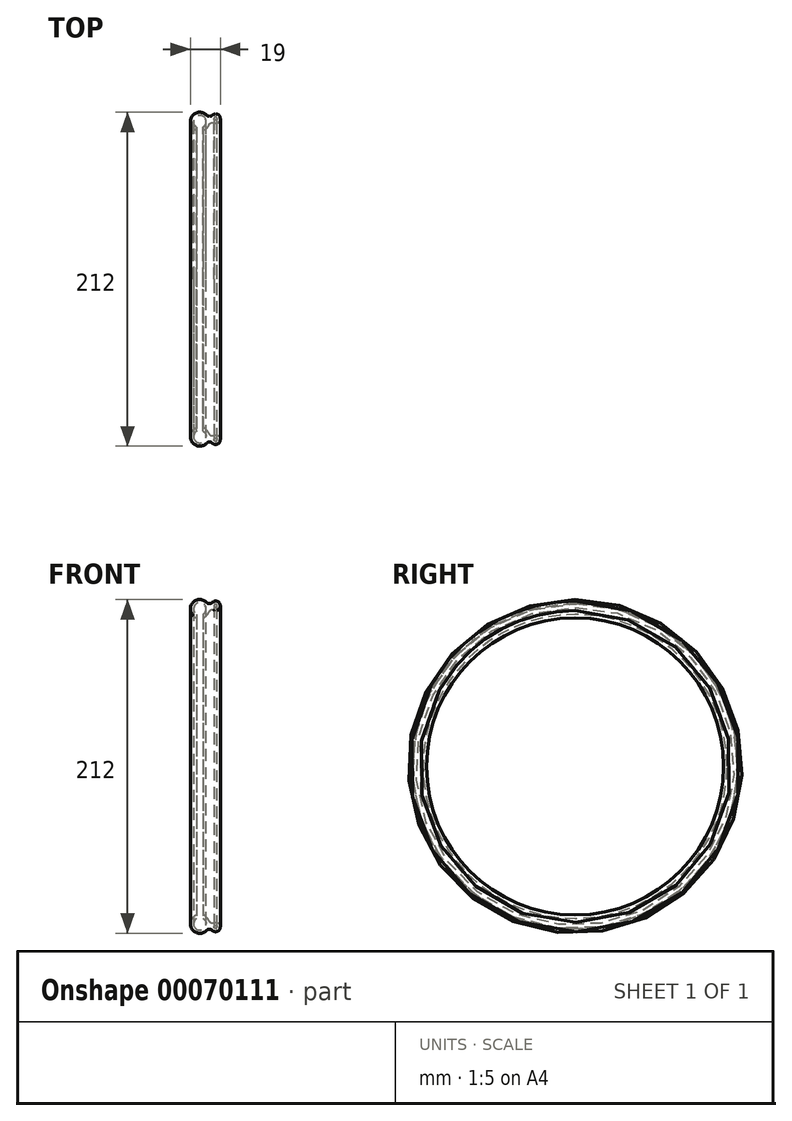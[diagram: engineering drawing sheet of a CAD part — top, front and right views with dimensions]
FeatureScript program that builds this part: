
annotation { "Feature Type Name" : "Feature", "Feature Type Description" : "" }
export const myFeature = defineFeature(function(context is Context, id is Id, definition is map)
    precondition{}
    {
        {
            var Q0;
            Q0=qCreatedBy(makeId("Front.planeOp"),FACE);
            var sketch = newSketch(context, id + "F0", { "sketchPlane" : qUnion([Q0])});
            skArc(sketch, "E0", {"start": v(2, -3.46) * mm, "mid": v(0, 4) * mm, "end": v(-2, -3.46) * mm});
            skArc(sketch, "E1", {"start": v(2, -5.66) * mm, "mid": v(4.17, -4.31) * mm, "end": v(5.59, -2.18) * mm});
            skLineSegment(sketch, "E2", {"start": v(-2, -3.46) * mm, "end": v(-2, -5.66) * mm});
            skLineSegment(sketch, "E3", {"start": v(2, -3.46) * mm, "end": v(2, -5.66) * mm});
            skCircle(sketch, "E4", {"center": v(10, 2) * mm, "radius": 1 * mm});
            skArc(sketch, "E5", {"start": v(8.86, -0.78) * mm, "mid": v(12.94, 2.59) * mm, "end": v(7.88, 4.13) * mm});
            skArc(sketch, "E6", {"start": v(4.32, 4.16) * mm, "mid": v(6.1, 3.4) * mm, "end": v(7.88, 4.13) * mm});
            skArc(sketch, "E7", {"start": v(8.86, -0.78) * mm, "mid": v(6.93, -0.8) * mm, "end": v(5.59, -2.18) * mm});
            skArc(sketch, "E8.trimOffspring", {"start": v(4.32, 4.16) * mm, "mid": v(-5.05, 3.25) * mm, "end": v(-2, -5.66) * mm});
            skLineSegment(sketch, "E9", {"start": v(0, -100) * mm, "end": v(29.48, -100) * mm});
            skSolve(sketch);
        }
        {
            var Q0;
            Q0 = qSketchRegion(id + "F0", true);
            var Q1;
            Q1=sQuery(id+"F0.wireOp",EDGE,"E9");
            revolve(context, id + "F1", {"entities" : qUnion([Q0]), "axis" : qUnion([Q1]), "revolveType" : RevolveType.FULL});
        }
    });
